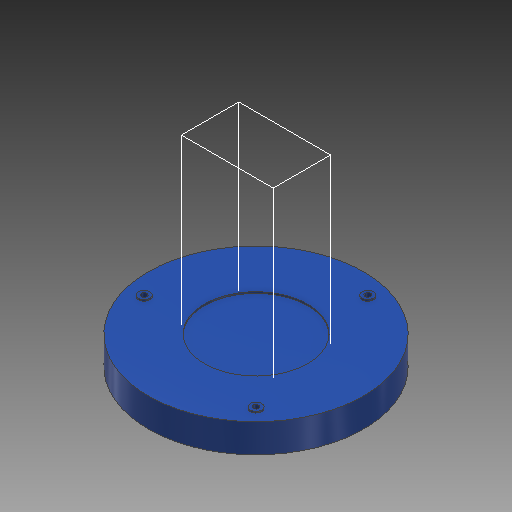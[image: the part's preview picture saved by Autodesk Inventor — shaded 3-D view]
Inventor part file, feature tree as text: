
AUTODESK INVENTOR PART (.ipt)
format: ipt  version: 2018 (Build 220112000, 112)  size: 302,592 bytes
history: native  units: mm
features: extrude x6, sketch x6, pattern_circular x2, shell x1
ambient origin geometry x8: Origin, YZ Plane, XZ Plane, XY Plane, X Axis, Y Axis, Z Axis, Center Point
bodies: 实体1 (feature_tree)
feature tree (15):
  extrude  "拉伸1"  Depth=17.0mm TaperAngle=0.0deg
  extrude  "拉伸3"  Depth=8.0mm
  shell  "抽壳1"  Thickness=35.0mm
  extrude  "拉伸5"  Depth=1.0mm TaperAngle=0.0deg
  extrude  "拉伸6"  Depth=1.8mm
  pattern_circular  "环形阵列1"  Count=5  [1 undecoded]
  extrude  "拉伸7"  Depth=2.0mm TaperAngle=0.0deg
  extrude  "拉伸8"  Depth=4.0mm TaperAngle=360.0deg
  pattern_circular  "环形阵列2"  [2 undecoded]
  sketch  "草图1"  dims[d0=135.0mm d1=17.0mm d2=0.0mm]
  sketch  "草图3"  dims[d3=100.0mm d8=8.0mm d9=35.0mm]
  sketch  "草图6"  dims[d10=35.0mm d11=1.0mm d12=0.0mm]
  sketch  "草图7"  dims[d13=1.8mm d17=72.0mm]
  sketch  "草图8"  dims[d18=1.0mm d19=0.0mm]
  sketch  "草图9"  dims[d25=10.0mm d26=50.0mm d27=2.0mm d28=0.0mm d29=30.0mm d30=360.0deg d32=4.0mm d33=3.0mm d34=0.0mm d35=4.0mm d36=3.0mm d37=0.0mm d39=30.0mm d40=360.0deg d42=60.0deg]
note: 3 required parameter values undecoded (feature->parameter linkage not recoverable at this tier; creation-order binding heuristic only, values carry confidence <= 0.55)
